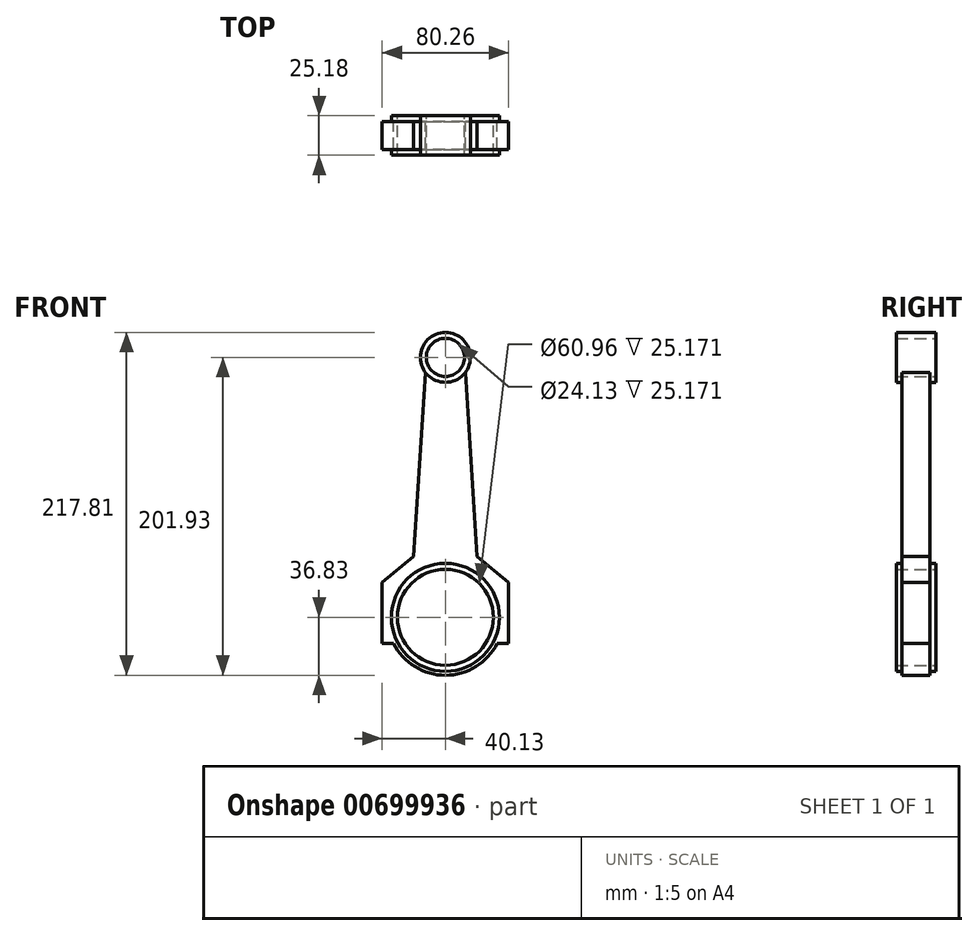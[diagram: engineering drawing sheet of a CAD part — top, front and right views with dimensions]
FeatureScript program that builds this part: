
annotation { "Feature Type Name" : "Feature", "Feature Type Description" : "" }
export const myFeature = defineFeature(function(context is Context, id is Id, definition is map)
    precondition{}
    {
        {
            var Q0;
            Q0=qCreatedBy(makeId("Front.planeOp"),FACE);
            var sketch = newSketch(context, id + "F0", { "sketchPlane" : qUnion([Q0])});
            skCircle(sketch, "E0", {"center": v(0, 165.1) * mm, "radius": 12.07 * mm});
            skCircle(sketch, "E1", {"center": v(0, 0) * mm, "radius": 30.48 * mm});
            skLineSegment(sketch, "E2", {"start": v(0, 0) * mm, "end": v(-40.13, 0) * mm});
            skLineSegment(sketch, "E3", {"start": v(-40.13, 0) * mm, "end": v(-40.13, 22.13) * mm});
            skLineSegment(sketch, "E4", {"start": v(-40.13, 22.13) * mm, "end": v(-20.24, 38.74) * mm});
            skLineSegment(sketch, "E5", {"start": v(-20.24, 38.74) * mm, "end": v(-12.04, 165.88) * mm});
            skCircle(sketch, "E6.0", {"center": v(0, 165.1) * mm, "radius": 15.88 * mm});
            skLineSegment(sketch, "E7.MirrorCS", {"start": v(20.24, 38.74) * mm, "end": v(12.04, 165.88) * mm});
            skLineSegment(sketch, "E8.MirrorCS", {"start": v(40.13, 22.13) * mm, "end": v(20.24, 38.74) * mm});
            skLineSegment(sketch, "E9.MirrorCS", {"start": v(40.13, 0) * mm, "end": v(40.13, 22.13) * mm});
            skLineSegment(sketch, "E10.MirrorCS", {"start": v(0, 0) * mm, "end": v(40.13, 0) * mm});
            skCircle(sketch, "E11.0", {"center": v(0, 0) * mm, "radius": 34.3 * mm});
            skArc(sketch, "E12.0", {"start": v(-32.92, -16.51) * mm, "mid": v(0, -36.83) * mm, "end": v(32.92, -16.5) * mm});
            skLineSegment(sketch, "E13", {"start": v(-40.13, 0) * mm, "end": v(-40.13, -16.51) * mm});
            skLineSegment(sketch, "E14", {"start": v(-40.13, -16.51) * mm, "end": v(-32.92, -16.51) * mm});
            skLineSegment(sketch, "E15.MirrorCS", {"start": v(40.13, -16.51) * mm, "end": v(32.92, -16.51) * mm});
            skLineSegment(sketch, "E16.MirrorCS", {"start": v(40.13, 0) * mm, "end": v(40.13, -16.51) * mm});
            skSolve(sketch);
        }
        {
            var Q0;
            {var subQ0=sQuery(id+"F0.wireOp",EDGE,"E2");var subQ1=sQuery(id+"F0.wireOp",EDGE,"E1");var subQ2=makeQuery(id+"F0.imprint","INTERSECT",VERTEX,{"derivedFrom":[subQ1,subQ0]});Q0=makeQuery(id+"F0.imprint","IMPRINT",FACE,{"disambiguationData":[TD([[makeQuery(id+"F0.imprint","IMPRINT",EDGE,{"disambiguationData":[TD([[subQ2,1.0]])],"derivedFrom":subQ1}),-1.0]])]});}
            extrude(context, id + "F1", {"entities" : qUnion([Q0]), "endBound" : BoundingType.SYMMETRIC, "depth" : 25.17 * mm, "offsetDistance" : 25.4 * mm});
        }
        {
            var Q0;
            {var subQ0=sQuery(id+"F0.wireOp",EDGE,"E5");var subQ1=sQuery(id+"F0.wireOp",EDGE,"E0");var subQ2=makeQuery(id+"F0.imprint","INTERSECT",VERTEX,{"derivedFrom":[subQ1,subQ0]});Q0=makeQuery(id+"F0.imprint","IMPRINT",FACE,{"disambiguationData":[TD([[makeQuery(id+"F0.imprint","IMPRINT",EDGE,{"disambiguationData":[TD([[subQ2,-1.0]])],"derivedFrom":subQ1}),-1.0]])]});}
            var Q1;
            {var subQ0=sQuery(id+"F0.wireOp",EDGE,"E5");var subQ1=sQuery(id+"F0.wireOp",EDGE,"E0");var subQ2=makeQuery(id+"F0.imprint","INTERSECT",VERTEX,{"derivedFrom":[subQ1,subQ0]});Q1=makeQuery(id+"F0.imprint","IMPRINT",FACE,{"disambiguationData":[TD([[makeQuery(id+"F0.imprint","IMPRINT",EDGE,{"disambiguationData":[TD([[subQ2,1.0]])],"derivedFrom":subQ1}),-1.0]])]});}
            extrude(context, id + "F2", {"entities" : qUnion([Q0, Q1]), "endBound" : BoundingType.SYMMETRIC, "depth" : 25.17 * mm, "offsetDistance" : 25.4 * mm});
        }
        {
            var Q0;
            {var subQ10=sQuery(id+"F0.wireOp",EDGE,"E3");Q0=makeQuery(id+"F0.imprint","IMPRINT",FACE,{"disambiguationData":[TD([[makeQuery(id+"F0.imprint","IMPRINT",EDGE,{"derivedFrom":subQ10}),-1.0]])]});}
            extrude(context, id + "F3", {"entities" : qUnion([Q0]), "operationType" : NewBodyOperationType.ADD, "endBound" : BoundingType.SYMMETRIC, "depth" : 17.78 * mm, "offsetDistance" : 25.4 * mm});
        }
        {
            var Q0;
            {var subQ0=sQuery(id+"F0.wireOp",EDGE,"E2");var subQ1=sQuery(id+"F0.wireOp",EDGE,"E1");var subQ2=makeQuery(id+"F0.imprint","INTERSECT",VERTEX,{"derivedFrom":[subQ1,subQ0]});Q0=makeQuery(id+"F0.imprint","IMPRINT",FACE,{"disambiguationData":[TD([[makeQuery(id+"F0.imprint","IMPRINT",EDGE,{"disambiguationData":[TD([[subQ2,-1.0]])],"derivedFrom":subQ1}),-1.0]])]});}
            extrude(context, id + "F4", {"entities" : qUnion([Q0]), "endBound" : BoundingType.SYMMETRIC, "depth" : 25.17 * mm, "offsetDistance" : 25.4 * mm});
        }
        {
            var Q0;
            Q0=makeQuery(id+"F0.imprint","IMPRINT",FACE,{"disambiguationData":[TD([[makeQuery(id+"F0.imprint","IMPRINT",EDGE,{"derivedFrom":sQuery(id+"F0.wireOp",EDGE,"E12.0")}),1.0]])]});
            extrude(context, id + "F5", {"entities" : qUnion([Q0]), "operationType" : NewBodyOperationType.ADD, "endBound" : BoundingType.SYMMETRIC, "depth" : 17.78 * mm, "offsetDistance" : 25.4 * mm});
        }
    });
